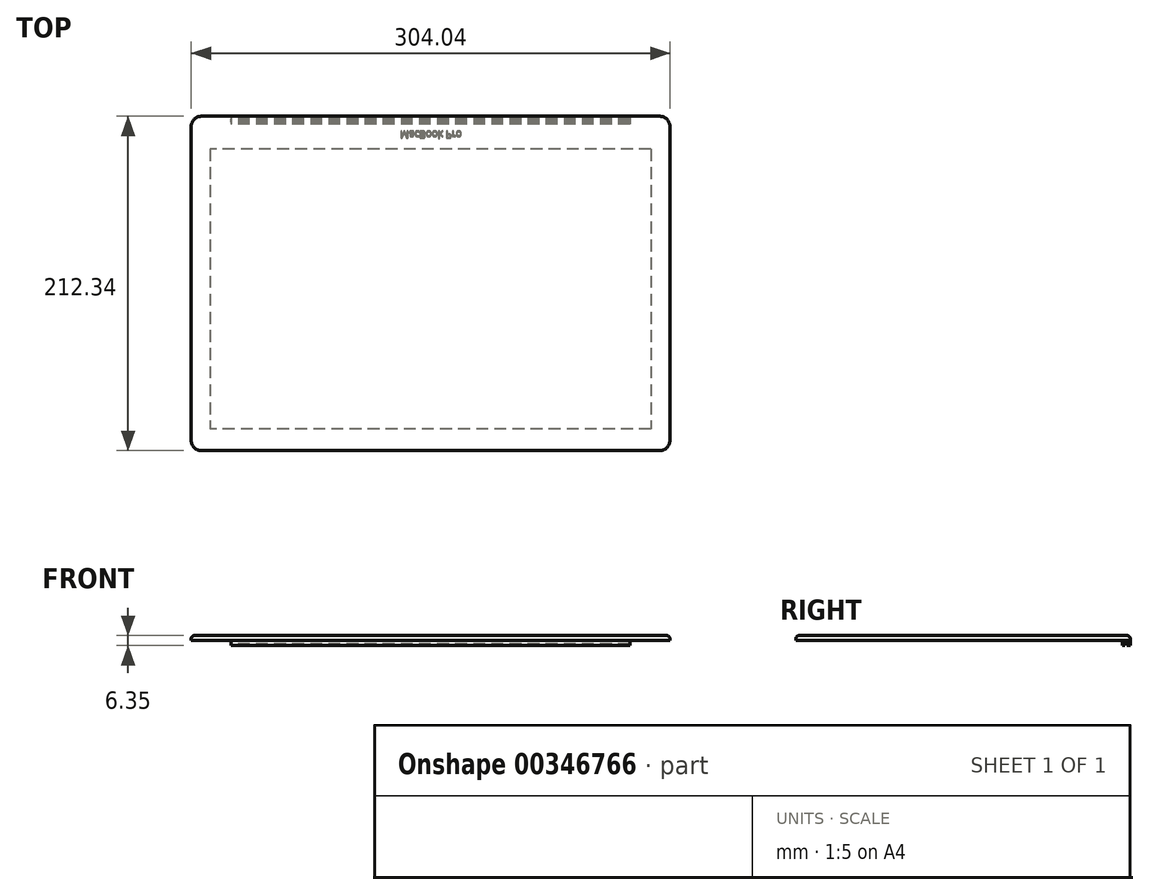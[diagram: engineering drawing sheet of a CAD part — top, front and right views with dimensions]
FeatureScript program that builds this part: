
annotation { "Feature Type Name" : "Feature", "Feature Type Description" : "" }
export const myFeature = defineFeature(function(context is Context, id is Id, definition is map)
    precondition{}
    {
        {
            var Q0;
            Q0=qCreatedBy(makeId("Top.planeOp"),FACE);
            var sketch = newSketch(context, id + "F0", { "sketchPlane" : qUnion([Q0])});
            skPoint(sketch, "E0.middle", {"position": v(0, 0) * mm});
            skLineSegment(sketch, "E1.bottom", {"start": v(145.67, -106.17) * mm, "end": v(-145.67, -106.17) * mm});
            skLineSegment(sketch, "E1.top", {"start": v(145.67, 106.17) * mm, "end": v(-145.67, 106.17) * mm});
            skLineSegment(sketch, "E1.left", {"start": v(152.02, -99.82) * mm, "end": v(152.02, 99.82) * mm});
            skLineSegment(sketch, "E1.right", {"start": v(-152.02, -99.82) * mm, "end": v(-152.02, 99.82) * mm});
            skPoint(sketch, "E2.visualSharp", {"position": v(152.02, 106.17) * mm});
            skArc(sketch, "E2.filletArc", {"start": v(152.02, 99.82) * mm, "mid": v(150.16, 104.31) * mm, "end": v(145.67, 106.17) * mm});
            skPoint(sketch, "E3.visualSharp", {"position": v(152.02, -106.17) * mm});
            skArc(sketch, "E3.filletArc", {"start": v(145.67, -106.17) * mm, "mid": v(150.16, -104.31) * mm, "end": v(152.02, -99.82) * mm});
            skPoint(sketch, "E4.visualSharp", {"position": v(-152.02, -106.17) * mm});
            skArc(sketch, "E4.filletArc", {"start": v(-152.02, -99.82) * mm, "mid": v(-150.16, -104.31) * mm, "end": v(-145.67, -106.17) * mm});
            skPoint(sketch, "E5.visualSharp", {"position": v(-152.02, 106.17) * mm});
            skArc(sketch, "E5.filletArc", {"start": v(-145.67, 106.17) * mm, "mid": v(-150.16, 104.31) * mm, "end": v(-152.02, 99.82) * mm});
            skSolve(sketch);
        }
        {
            var Q0;
            Q0 = qSketchRegion(id + "F0", true);
            extrude(context, id + "F1", {"entities" : qUnion([Q0]), "depth" : 3.05 * mm});
        }
        {
            var Q0;
            Q0=makeQuery(id+"F1.opExtrude","CAP_FACE",FACE,{"disambiguationData":[OSD([sQuery(id+"F0.wireOp",EDGE,"E1.bottom"),sQuery(id+"F0.wireOp",EDGE,"E1.top"),sQuery(id+"F0.wireOp",EDGE,"E1.left"),sQuery(id+"F0.wireOp",EDGE,"E1.right"),sQuery(id+"F0.wireOp",EDGE,"E2.filletArc"),sQuery(id+"F0.wireOp",EDGE,"E3.filletArc"),sQuery(id+"F0.wireOp",EDGE,"E4.filletArc"),sQuery(id+"F0.wireOp",EDGE,"E5.filletArc")])],"isStart":false});
            fillet(context, id + "F2", {"entities" : qUnion([Q0]), "radius" : 2.03 * mm, "tangentPropagation" : true, "allowEdgeOverflow" : false});
        }
        {
            var Q0;
            Q0=makeQuery(id+"F1.opExtrude","CAP_FACE",FACE,{"disambiguationData":[OSD([sQuery(id+"F0.wireOp",EDGE,"E1.bottom"),sQuery(id+"F0.wireOp",EDGE,"E1.top"),sQuery(id+"F0.wireOp",EDGE,"E1.left"),sQuery(id+"F0.wireOp",EDGE,"E1.right"),sQuery(id+"F0.wireOp",EDGE,"E2.filletArc"),sQuery(id+"F0.wireOp",EDGE,"E3.filletArc"),sQuery(id+"F0.wireOp",EDGE,"E4.filletArc"),sQuery(id+"F0.wireOp",EDGE,"E5.filletArc")])],"isStart":true});
            var sketch = newSketch(context, id + "F3", { "sketchPlane" : qUnion([Q0])});
            skLineSegment(sketch, "E6.0", {"start": v(145.67, 106.17) * mm, "end": v(-145.67, 106.17) * mm});
            skArc(sketch, "E7.0", {"start": v(145.67, 106.17) * mm, "mid": v(150.16, 104.31) * mm, "end": v(152.02, 99.82) * mm});
            skLineSegment(sketch, "E8.0", {"start": v(152.02, 99.82) * mm, "end": v(152.02, -99.82) * mm});
            skArc(sketch, "E9.0", {"start": v(152.02, -99.82) * mm, "mid": v(150.16, -104.31) * mm, "end": v(145.67, -106.17) * mm});
            skLineSegment(sketch, "E10.0", {"start": v(145.67, -106.17) * mm, "end": v(-145.67, -106.17) * mm});
            skArc(sketch, "E11.0", {"start": v(-145.67, -106.17) * mm, "mid": v(-150.16, -104.31) * mm, "end": v(-152.02, -99.82) * mm});
            skLineSegment(sketch, "E12.0", {"start": v(-152.02, 99.82) * mm, "end": v(-152.02, -99.82) * mm});
            skArc(sketch, "E13.0", {"start": v(-152.02, 99.82) * mm, "mid": v(-150.16, 104.31) * mm, "end": v(-145.67, 106.17) * mm});
            skLineSegment(sketch, "E14.1", {"start": v(150.75, 99.82) * mm, "end": v(150.75, -97.15) * mm});
            skLineSegment(sketch, "E14.2", {"start": v(144.4, -103.5) * mm, "end": v(-144.4, -103.5) * mm});
            skLineSegment(sketch, "E14.3", {"start": v(-150.75, 98.55) * mm, "end": v(-150.75, -97.15) * mm});
            skArc(sketch, "E15", {"start": v(-144.4, 104.9) * mm, "mid": v(-148.89, 103.04) * mm, "end": v(-150.75, 98.55) * mm});
            skArc(sketch, "E16", {"start": v(150.75, 99.82) * mm, "mid": v(148.54, 103.47) * mm, "end": v(144.53, 104.9) * mm});
            skLineSegment(sketch, "E17.trimOffspring", {"start": v(144.53, 104.9) * mm, "end": v(-144.4, 104.9) * mm});
            skArc(sketch, "E18", {"start": v(144.4, -103.5) * mm, "mid": v(148.89, -101.64) * mm, "end": v(150.75, -97.15) * mm});
            skArc(sketch, "E19", {"start": v(-150.75, -97.15) * mm, "mid": v(-148.89, -101.64) * mm, "end": v(-144.4, -103.5) * mm});
            skSolve(sketch);
        }
        {
            var Q0;
            Q0=makeQuery(id+"F3.imprint","IMPRINT",FACE,{"disambiguationData":[TD([[makeQuery(id+"F3.imprint","IMPRINT",EDGE,{"derivedFrom":sQuery(id+"F3.wireOp",EDGE,"E14.1")}),-1.0]])]});
            extrude(context, id + "F4", {"entities" : qUnion([Q0]), "operationType" : NewBodyOperationType.ADD, "oppositeDirection" : true, "depth" : 0.1 * mm});
        }
        {
            var Q0;
            Q0=makeQuery(id+"F1.opExtrude","CAP_FACE",FACE,{"disambiguationData":[OSD([sQuery(id+"F0.wireOp",EDGE,"E1.bottom"),sQuery(id+"F0.wireOp",EDGE,"E1.top"),sQuery(id+"F0.wireOp",EDGE,"E1.left"),sQuery(id+"F0.wireOp",EDGE,"E1.right"),sQuery(id+"F0.wireOp",EDGE,"E2.filletArc"),sQuery(id+"F0.wireOp",EDGE,"E3.filletArc"),sQuery(id+"F0.wireOp",EDGE,"E4.filletArc"),sQuery(id+"F0.wireOp",EDGE,"E5.filletArc")])],"isStart":true});
            var sketch = newSketch(context, id + "F5", { "sketchPlane" : qUnion([Q0])});
            skLineSegment(sketch, "E20.bottom", {"start": v(140.03, -85.35) * mm, "end": v(-140.03, -85.35) * mm});
            skLineSegment(sketch, "E20.top", {"start": v(140.03, 92.45) * mm, "end": v(-140.03, 92.45) * mm});
            skLineSegment(sketch, "E20.left", {"start": v(140.03, -85.35) * mm, "end": v(140.03, 92.45) * mm});
            skLineSegment(sketch, "E20.right", {"start": v(-140.03, -85.35) * mm, "end": v(-140.03, 92.45) * mm});
            skPoint(sketch, "E20.middle", {"position": v(0, 3.55) * mm});
            skSolve(sketch);
        }
        {
            var Q0;
            Q0 = qSketchRegion(id + "F5", true);
            extrude(context, id + "F6", {"entities" : qUnion([Q0]), "operationType" : NewBodyOperationType.ADD, "depth" : 0 * mm});
        }
        {
            var Q0;
            Q0=makeQuery(id+"F1.opExtrude","CAP_FACE",FACE,{"disambiguationData":[OSD([sQuery(id+"F0.wireOp",EDGE,"E1.bottom"),sQuery(id+"F0.wireOp",EDGE,"E1.top"),sQuery(id+"F0.wireOp",EDGE,"E1.left"),sQuery(id+"F0.wireOp",EDGE,"E1.right"),sQuery(id+"F0.wireOp",EDGE,"E2.filletArc"),sQuery(id+"F0.wireOp",EDGE,"E3.filletArc"),sQuery(id+"F0.wireOp",EDGE,"E4.filletArc"),sQuery(id+"F0.wireOp",EDGE,"E5.filletArc")])],"isStart":true});
            var sketch = newSketch(context, id + "F7", { "sketchPlane" : qUnion([Q0])});
            skText(sketch, "E21", { "text": "MacBook Pro", "fontName": "OpenSans-Regular.ttf"});
            const initialGuessF7  = {"E21": [-0.01945, -0.09677, 1, 0, 0.00457]};
            skSetInitialGuess(sketch, initialGuessF7);
            skSolve(sketch);
        }
        {
            var Q0;
            Q0 = qSketchRegion(id + "F7", true);
            extrude(context, id + "F8", {"entities" : qUnion([Q0]), "operationType" : NewBodyOperationType.ADD, "depth" : 0 * mm});
        }
        {
            var Q0;
            Q0=makeQuery(id+"F1.opExtrude","CAP_FACE",FACE,{"disambiguationData":[OSD([sQuery(id+"F0.wireOp",EDGE,"E1.bottom"),sQuery(id+"F0.wireOp",EDGE,"E1.top"),sQuery(id+"F0.wireOp",EDGE,"E1.left"),sQuery(id+"F0.wireOp",EDGE,"E1.right"),sQuery(id+"F0.wireOp",EDGE,"E2.filletArc"),sQuery(id+"F0.wireOp",EDGE,"E3.filletArc"),sQuery(id+"F0.wireOp",EDGE,"E4.filletArc"),sQuery(id+"F0.wireOp",EDGE,"E5.filletArc")])],"isStart":true});
            var sketch = newSketch(context, id + "F9", { "sketchPlane" : qUnion([Q0])});
            skLineSegment(sketch, "E22.bottom", {"start": v(126.62, -106.17) * mm, "end": v(-126.62, -106.17) * mm});
            skLineSegment(sketch, "E22.top", {"start": v(126.62, -101.1) * mm, "end": v(-126.62, -101.1) * mm});
            skLineSegment(sketch, "E22.left", {"start": v(126.62, -106.17) * mm, "end": v(126.62, -101.1) * mm});
            skLineSegment(sketch, "E22.right", {"start": v(-126.62, -106.17) * mm, "end": v(-126.62, -101.1) * mm});
            skPoint(sketch, "E22.middle", {"position": v(0, -103.63) * mm});
            skLineSegment(sketch, "E23", {"start": v(0, 29.43) * mm, "end": v(0, -119.12) * mm, "construction": true});
            skSolve(sketch);
        }
        {
            var Q0;
            Q0 = qSketchRegion(id + "F9", true);
            extrude(context, id + "F10", {"entities" : qUnion([Q0]), "operationType" : NewBodyOperationType.ADD, "depth" : 3.3 * mm});
        }
        {
            var Q0;
            Q0=makeQuery(id+"F10.opExtrude","SWEPT_FACE",FACE,{"disambiguationData":[OSD([sQuery(id+"F9.wireOp",EDGE,"E22.right")])]});
            var sketch = newSketch(context, id + "F11", { "sketchPlane" : qUnion([Q0])});
            skArc(sketch, "E24", {"start": v(-102.8, -2.32) * mm, "mid": v(-103.5, -0.47) * mm, "end": v(-104.19, -2.32) * mm});
            skLineSegment(sketch, "E25.bottom", {"start": v(-104.19, -3.3) * mm, "end": v(-102.8, -3.3) * mm});
            skLineSegment(sketch, "E25.left", {"start": v(-104.19, -3.3) * mm, "end": v(-104.19, -2.32) * mm});
            skLineSegment(sketch, "E25.right", {"start": v(-102.8, -3.3) * mm, "end": v(-102.8, -2.32) * mm});
            skPoint(sketch, "E25.top.end.orphan", {"position": v(-102.8, 0.25) * mm});
            skPoint(sketch, "E25.top.start.orphan", {"position": v(-104.19, 0.25) * mm});
            skSolve(sketch);
        }
        {
            var Q0;
            Q0 = qSketchRegion(id + "F11", true);
            var Q1;
            Q1=makeQuery(id+"F10.opExtrude","SWEPT_FACE",FACE,{"disambiguationData":[OSD([sQuery(id+"F9.wireOp",EDGE,"E22.left")])]});
            extrude(context, id + "F12", {"entities" : qUnion([Q0]), "operationType" : NewBodyOperationType.REMOVE, "endBound" : BoundingType.UP_TO_SURFACE, "oppositeDirection" : true, "endBoundEntityFace" : qUnion([Q1]), "depth" : 25.4 * mm});
        }
    });
